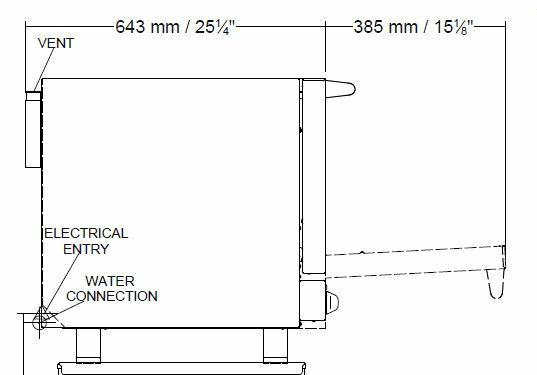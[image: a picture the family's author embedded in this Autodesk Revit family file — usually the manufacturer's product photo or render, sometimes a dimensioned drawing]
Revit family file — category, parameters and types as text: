
# Revit family: QF_MOFFAT_E27D2_NZ
name_source: partatom
category: Specialty Equipment
revit_build: Autodesk Revit 2014 (Build: 20130308_1515(x64)
units: mm (PartAtom-declared; Revit-internal decimal feet)

## types (1)
- QF_MOFFAT_E27D2_NZ
    Apparent Power = 2760 VA
    Cold Water Connection Height = 0 mm  [stored 0 ft]
    Cold Water Flow = 0 GPM
    Cold Water Maximum Pressure = 80.00 psi
    Cold Water Minimum Pressure = 20.00 psi
    Cold Water RI Height = 0 mm  [stored 0 ft]
    Cold Water Size = 1"
    Cold Water Temperature Recommended = 0 °F
    Conn Conduit = Yes
    Cycle = 50 Hz
    Depth = 762 mm  [stored 2.5 ft]
    Description = FULL SIZE DIGITAL / ELECTRIC CONVECTION OVEN ON A STAINLESS STEEL STAND
    Elec Conn Connection Height = 0 mm  [stored 0 ft]
    Elec Conn RI Height = 0 mm  [stored 0 ft]
    Electrical Remarks = 230-240V, 50Hz, 1P+N+E, 3kW, 12A
    Exhaust RI Height = 0 mm  [stored 0 ft]
    Exhaust Static Press = 0.00 in-wg
    Exhaust Vent Depth = 0 mm  [stored 0 ft]
    Exhaust Vent Diameter = 0 mm  [stored 0 ft]
    Exhaust Vent Width = 0 mm  [stored 0 ft]
    Exhaust Volume = 0 CFM
    FL Amps = 12 A
    Foodservice Equipment Identifier = Yes
    Height = 1487 mm  [stored 4.87861 ft]
    Height of Stand = 880 mm  [stored 2.88714 ft]
    Identify Quantity as Lot = Yes
    Length = 810 mm
    Manufacturer = MOFFAT
    Max Overcurrent Protection = 0 A
    Min Ckt Ampacity = 0 A
    Model = E27D2
    Number of Poles = 1
    Phase = 1
    URL = www.moffat.com.au
    URL Cutsheet = www.moffat.com.au
    Volts = 230 V
    Watts = 3000 W
    Weight in Pounds = 0

note: [stored X ft] marks values corroborated as IEEE doubles in the binary element streams (Revit-internal decimal feet)

## geometry (parser evidence)
native form markers: Blend x12, Sweep x9
no freeform markers — native parametric forms only
